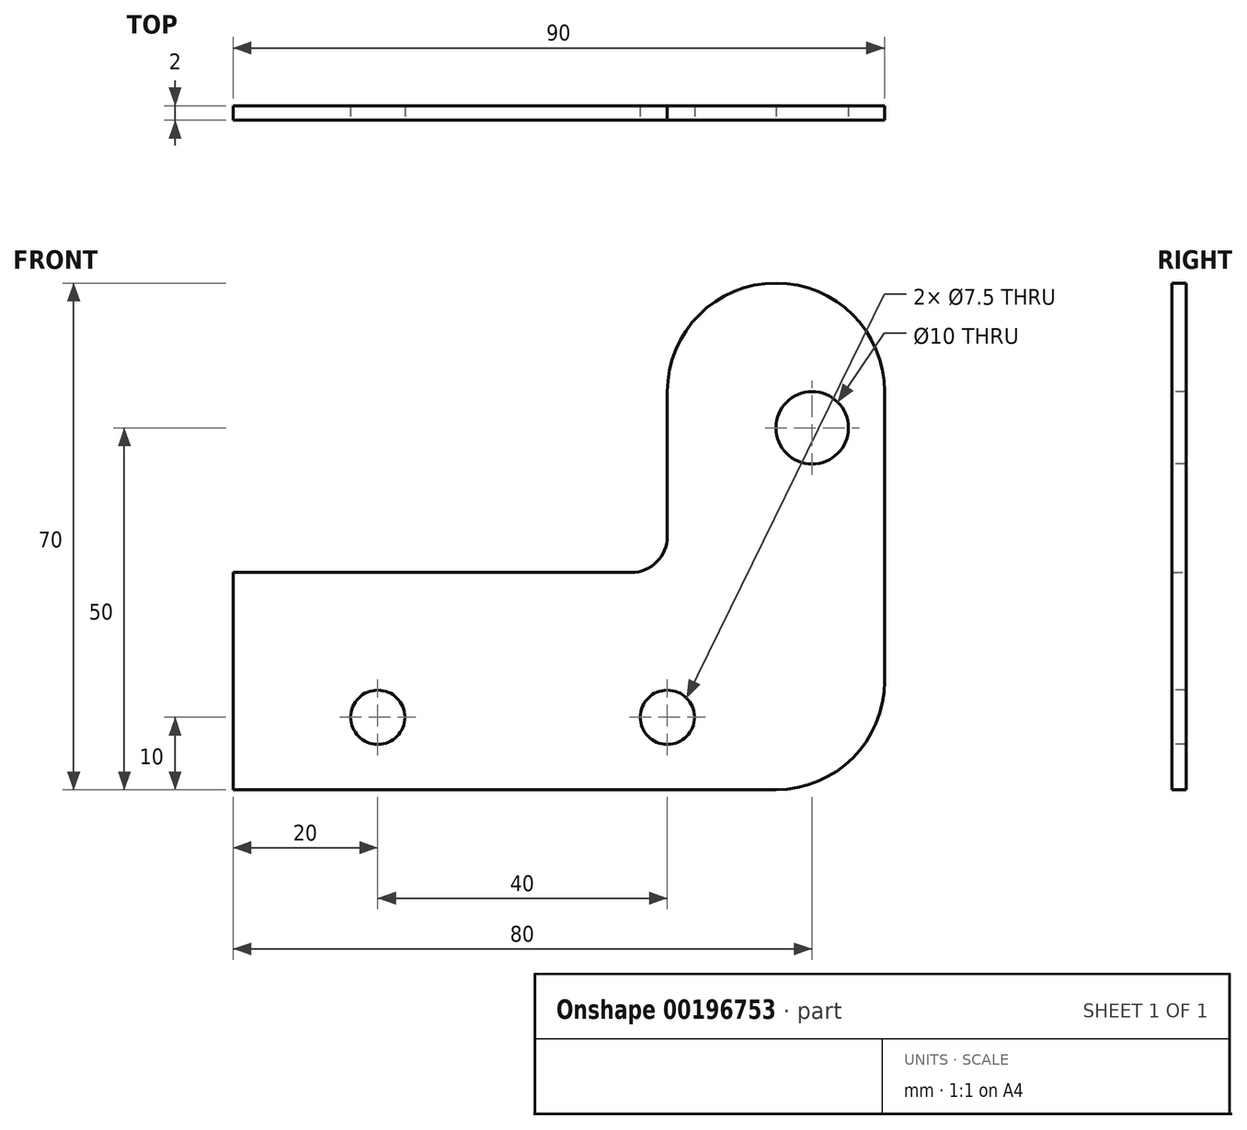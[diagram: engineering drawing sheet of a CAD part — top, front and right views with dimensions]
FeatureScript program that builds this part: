
annotation { "Feature Type Name" : "Feature", "Feature Type Description" : "" }
export const myFeature = defineFeature(function(context is Context, id is Id, definition is map)
    precondition{}
    {
        {
            var Q0;
            Q0=qCreatedBy(makeId("Front.planeOp"),FACE);
            var sketch = newSketch(context, id + "F0", { "sketchPlane" : qUnion([Q0])});
            skLineSegment(sketch, "E0.bottom", {"start": v(0, 0) * mm, "end": v(75, 0) * mm});
            skLineSegment(sketch, "E0.top", {"start": v(75, 70) * mm, "end": v(75, 70) * mm});
            skLineSegment(sketch, "E0.right", {"start": v(90, 15) * mm, "end": v(90, 55) * mm});
            skPoint(sketch, "E1.visualSharp", {"position": v(90, 0) * mm});
            skArc(sketch, "E1.filletArc", {"start": v(75, 0) * mm, "mid": v(85.6, 4.4) * mm, "end": v(90, 15) * mm});
            skPoint(sketch, "E2.visualSharp", {"position": v(90, 70) * mm});
            skArc(sketch, "E2.filletArc", {"start": v(90, 55) * mm, "mid": v(85.6, 65.6) * mm, "end": v(75, 70) * mm});
            skLineSegment(sketch, "E3", {"start": v(0, 0) * mm, "end": v(0, 30) * mm});
            skLineSegment(sketch, "E4", {"start": v(0, 30) * mm, "end": v(55, 30) * mm});
            skLineSegment(sketch, "E5", {"start": v(60, 35) * mm, "end": v(60, 55) * mm});
            skArc(sketch, "E6.filletArc", {"start": v(75, 70) * mm, "mid": v(64.4, 65.6) * mm, "end": v(60, 55) * mm});
            skPoint(sketch, "E7.visualSharp", {"position": v(60, 30) * mm});
            skArc(sketch, "E7.filletArc", {"start": v(55, 30) * mm, "mid": v(58.54, 31.46) * mm, "end": v(60, 35) * mm});
            skSolve(sketch);
        }
        {
            var Q0;
            Q0=makeQuery(id+"F0.imprint","IMPRINT",FACE,{"disambiguationData":[TD([[makeQuery(id+"F0.imprint","IMPRINT",EDGE,{"derivedFrom":sQuery(id+"F0.wireOp",EDGE,"E0.bottom")}),1.0]])]});
            extrude(context, id + "F1", {"entities" : qUnion([Q0]), "depth" : 2 * mm});
        }
        {
            var Q0;
            Q0=makeQuery(id+"F1.opExtrude","CAP_FACE",FACE,{"disambiguationData":[OSD([sQuery(id+"F0.wireOp",EDGE,"E0.bottom"),sQuery(id+"F0.wireOp",EDGE,"E0.top"),sQuery(id+"F0.wireOp",EDGE,"E0.left"),sQuery(id+"F0.wireOp",EDGE,"E0.right")])],"isStart":false});
            var sketch = newSketch(context, id + "F2", { "sketchPlane" : qUnion([Q0])});
            skLineSegment(sketch, "E8", {"start": v(0, 0) * mm, "end": v(0, 10) * mm});
            skCircle(sketch, "E9", {"center": v(20, 10) * mm, "radius": 3.75 * mm});
            skCircle(sketch, "E10", {"center": v(60, 10) * mm, "radius": 3.75 * mm});
            skCircle(sketch, "E11", {"center": v(80, 50) * mm, "radius": 5 * mm});
            skSolve(sketch);
        }
        {
            var Q0;
            Q0 = qSketchRegion(id + "F2", true);
            extrude(context, id + "F3", {"entities" : qUnion([Q0]), "operationType" : NewBodyOperationType.REMOVE, "oppositeDirection" : true, "depth" : 25 * mm});
        }
    });
